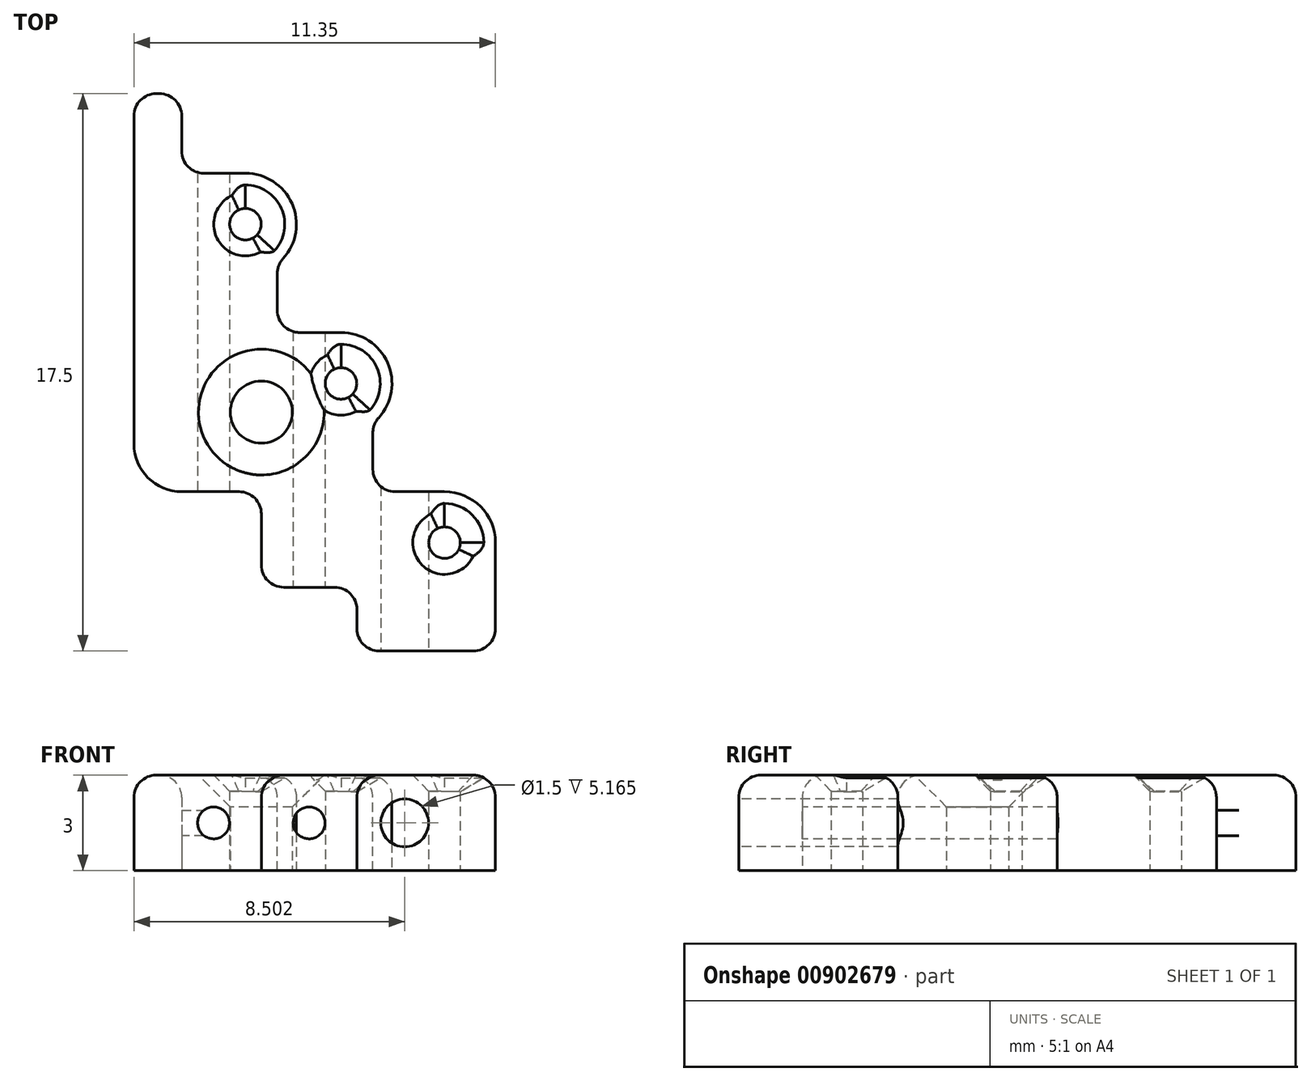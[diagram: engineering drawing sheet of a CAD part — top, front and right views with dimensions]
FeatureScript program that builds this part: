
annotation { "Feature Type Name" : "Feature", "Feature Type Description" : "" }
export const myFeature = defineFeature(function(context is Context, id is Id, definition is map)
    precondition{}
    {
        {
            var Q0;
            Q0=qCreatedBy(makeId("Top.planeOp"),FACE);
            var sketch = newSketch(context, id + "F0", { "sketchPlane" : qUnion([Q0])});
            skLineSegment(sketch, "E0.bottom", {"start": v(-17.84, 17.5) * mm, "end": v(-16.34, 17.5) * mm});
            skLineSegment(sketch, "E0.top", {"start": v(-10.84, 0) * mm, "end": v(-6.34, 0) * mm});
            skLineSegment(sketch, "E0.left", {"start": v(-17.84, 17.5) * mm, "end": v(-17.84, 6.5) * mm});
            skLineSegment(sketch, "E1", {"start": v(-14.34, 15) * mm, "end": v(-16.34, 15) * mm});
            skLineSegment(sketch, "E2", {"start": v(-13.34, 10) * mm, "end": v(-11.34, 10) * mm});
            skLineSegment(sketch, "E3", {"start": v(-10.34, 5) * mm, "end": v(-8.09, 5) * mm});
            skLineSegment(sketch, "E4", {"start": v(-9.34, 0) * mm, "end": v(-9.34, 5) * mm, "construction": true});
            skLineSegment(sketch, "E5", {"start": v(-12.34, 10) * mm, "end": v(-12.34, -0.79) * mm, "construction": true});
            skPoint(sketch, "E6.visualSharp", {"position": v(-6.34, 0) * mm});
            skLineSegment(sketch, "E7", {"start": v(-15.34, 0) * mm, "end": v(-15.34, 15) * mm, "construction": true});
            skLineSegment(sketch, "E8", {"start": v(-13.84, 2) * mm, "end": v(-10.84, 2) * mm});
            skLineSegment(sketch, "E9", {"start": v(-16.34, 5) * mm, "end": v(-13.84, 5) * mm});
            skLineSegment(sketch, "E10", {"start": v(-10.84, 2) * mm, "end": v(-10.84, 0) * mm});
            skLineSegment(sketch, "E11", {"start": v(-13.84, 5) * mm, "end": v(-13.84, 2) * mm});
            skCircle(sketch, "E12", {"center": v(-14.34, 13.4) * mm, "radius": 0.5 * mm});
            skPoint(sketch, "E13.visualSharp", {"position": v(-17.84, 17.5) * mm});
            skArc(sketch, "E14.filletArc", {"start": v(-17.84, 6.5) * mm, "mid": v(-17.4, 5.44) * mm, "end": v(-16.34, 5) * mm});
            skPoint(sketch, "E15.visualSharp", {"position": v(-10.84, 0) * mm});
            skCircle(sketch, "E16", {"center": v(-13.84, 7.5) * mm, "radius": 0.97 * mm});
            skCircle(sketch, "E17", {"center": v(-13.84, 7.5) * mm, "radius": 1.8 * mm, "construction": true});
            skLineSegment(sketch, "E18", {"start": v(-16.34, 15) * mm, "end": v(-16.34, 17.5) * mm});
            skLineSegment(sketch, "E19", {"start": v(-13.34, 10) * mm, "end": v(-13.34, 12.15) * mm});
            skLineSegment(sketch, "E20", {"start": v(-10.34, 5) * mm, "end": v(-10.34, 7.15) * mm});
            skCircle(sketch, "E21", {"center": v(-8.09, 3.4) * mm, "radius": 0.5 * mm});
            skLineSegment(sketch, "E22.trimOffspring", {"start": v(-6.49, 3.4) * mm, "end": v(-6.49, 0) * mm});
            skArc(sketch, "E23", {"start": v(-6.49, 3.4) * mm, "mid": v(-6.96, 4.53) * mm, "end": v(-8.09, 5) * mm});
            skCircle(sketch, "E24", {"center": v(-11.34, 8.4) * mm, "radius": 0.5 * mm});
            skArc(sketch, "E25", {"start": v(-10.34, 7.15) * mm, "mid": v(-9.83, 8.93) * mm, "end": v(-11.34, 10) * mm});
            skArc(sketch, "E26", {"start": v(-13.34, 12.15) * mm, "mid": v(-12.83, 13.93) * mm, "end": v(-14.34, 15) * mm});
            skSolve(sketch);
        }
        {
            var Q0;
            Q0=makeQuery(id+"F0.imprint","IMPRINT",FACE,{"disambiguationData":[TD([[makeQuery(id+"F0.imprint","IMPRINT",EDGE,{"derivedFrom":sQuery(id+"F0.wireOp",EDGE,"E0.bottom")}),-1.0]])]});
            extrude(context, id + "F1", {"entities" : qUnion([Q0]), "depth" : 3 * mm, "offsetDistance" : 25 * mm});
        }
        {
            var Q0;
            Q0=qCreatedBy(makeId("Front.planeOp"),FACE);
            var sketch = newSketch(context, id + "F2", { "sketchPlane" : qUnion([Q0])});
            skLineSegment(sketch, "E27.direction1", {"start": v(-9.34, 1.5) * mm, "end": v(-12.34, 1.5) * mm, "construction": true});
            skCircle(sketch, "E28", {"center": v(-9.34, 1.5) * mm, "radius": 0.75 * mm});
            skCircle(sketch, "E29", {"center": v(-12.34, 1.5) * mm, "radius": 0.5 * mm});
            skCircle(sketch, "E30.1.0.0", {"center": v(-15.34, 1.5) * mm, "radius": 0.5 * mm});
            skLineSegment(sketch, "E30.direction1", {"start": v(-12.34, 1.5) * mm, "end": v(-15.34, 1.5) * mm, "construction": true});
            skSolve(sketch);
        }
        {
            var Q0;
            Q0=makeQuery(id+"F2.imprint","IMPRINT",FACE,{"disambiguationData":[TD([[makeQuery(id+"F2.imprint","IMPRINT",EDGE,{"derivedFrom":sQuery(id+"F2.wireOp",EDGE,"E30.1.0.0")}),1.0]])]});
            extrude(context, id + "F3", {"entities" : qUnion([Q0]), "operationType" : NewBodyOperationType.REMOVE, "oppositeDirection" : true, "depth" : 25 * mm, "offsetDistance" : 25 * mm});
        }
        {
            var Q0;
            Q0=makeQuery(id+"F1.opExtrude","SWEPT_EDGE",EDGE,{"disambiguationData":[OSD([sQuery(id+"F0.wireOp",EDGE,"E0.bottom"),sQuery(id+"F0.wireOp",EDGE,"E18")])]});
            var Q1;
            Q1=makeQuery(id+"F1.opExtrude","SWEPT_EDGE",EDGE,{"disambiguationData":[OSD([sQuery(id+"F0.wireOp",EDGE,"E1"),sQuery(id+"F0.wireOp",EDGE,"E18")])]});
            var Q2;
            Q2=makeQuery(id+"F1.opExtrude","SWEPT_EDGE",EDGE,{"disambiguationData":[OSD([sQuery(id+"F0.wireOp",EDGE,"E19"),sQuery(id+"F0.wireOp",EDGE,"94513b36-e973-4ffa-a5f9-f9be3b932b12.trimOffspring")])]});
            var Q3;
            Q3=makeQuery(id+"F1.opExtrude","SWEPT_EDGE",EDGE,{"disambiguationData":[OSD([sQuery(id+"F0.wireOp",EDGE,"E1"),sQuery(id+"F0.wireOp",EDGE,"94513b36-e973-4ffa-a5f9-f9be3b932b12.trimOffspring")])]});
            var Q4;
            Q4=makeQuery(id+"F1.opExtrude","SWEPT_EDGE",EDGE,{"disambiguationData":[OSD([sQuery(id+"F0.wireOp",EDGE,"E2"),sQuery(id+"F0.wireOp",EDGE,"E25")])]});
            var Q5;
            Q5=makeQuery(id+"F1.opExtrude","SWEPT_EDGE",EDGE,{"disambiguationData":[OSD([sQuery(id+"F0.wireOp",EDGE,"E2"),sQuery(id+"F0.wireOp",EDGE,"E19")])]});
            var Q6;
            Q6=makeQuery(id+"F1.opExtrude","SWEPT_EDGE",EDGE,{"disambiguationData":[OSD([sQuery(id+"F0.wireOp",EDGE,"E20"),sQuery(id+"F0.wireOp",EDGE,"E25")])]});
            var Q7;
            Q7=makeQuery(id+"F1.opExtrude","SWEPT_EDGE",EDGE,{"disambiguationData":[OSD([sQuery(id+"F0.wireOp",EDGE,"E3"),sQuery(id+"F0.wireOp",EDGE,"E20")])]});
            var Q8;
            Q8=makeQuery(id+"F1.opExtrude","SWEPT_EDGE",EDGE,{"disambiguationData":[OSD([sQuery(id+"F0.wireOp",EDGE,"E22.trimOffspring"),sQuery(id+"F0.wireOp",EDGE,"E23")])]});
            var Q9;
            Q9=makeQuery(id+"F1.opExtrude","SWEPT_EDGE",EDGE,{"disambiguationData":[OSD([sQuery(id+"F0.wireOp",EDGE,"E0.top"),sQuery(id+"F0.wireOp",EDGE,"E22.trimOffspring")])]});
            var Q10;
            Q10=makeQuery(id+"F1.opExtrude","SWEPT_EDGE",EDGE,{"disambiguationData":[OSD([sQuery(id+"F0.wireOp",EDGE,"E0.top"),sQuery(id+"F0.wireOp",EDGE,"E10")])]});
            var Q11;
            Q11=makeQuery(id+"F1.opExtrude","SWEPT_EDGE",EDGE,{"disambiguationData":[OSD([sQuery(id+"F0.wireOp",EDGE,"E8"),sQuery(id+"F0.wireOp",EDGE,"E10")])]});
            var Q12;
            Q12=makeQuery(id+"F1.opExtrude","SWEPT_EDGE",EDGE,{"disambiguationData":[OSD([sQuery(id+"F0.wireOp",EDGE,"E8"),sQuery(id+"F0.wireOp",EDGE,"E11")])]});
            var Q13;
            Q13=makeQuery(id+"F1.opExtrude","SWEPT_EDGE",EDGE,{"disambiguationData":[OSD([sQuery(id+"F0.wireOp",EDGE,"E9"),sQuery(id+"F0.wireOp",EDGE,"E11")])]});
            var Q14;
            Q14=makeQuery(id+"F1.opExtrude","SWEPT_EDGE",EDGE,{"disambiguationData":[OSD([sQuery(id+"F0.wireOp",EDGE,"E0.bottom"),sQuery(id+"F0.wireOp",EDGE,"E0.left")])]});
            fillet(context, id + "F4", {"entities" : qUnion([Q0, Q1, Q2, Q3, Q4, Q5, Q6, Q7, Q8, Q9, Q10, Q11, Q12, Q13, Q14]), "radius" : 0.7 * mm, "tangentPropagation" : true, "allowEdgeOverflow" : false});
        }
        {
            var Q0;
            Q0=makeQuery(id+"F1.opExtrude","CAP_EDGE",EDGE,{"disambiguationData":[OSD([sQuery(id+"F0.wireOp",EDGE,"E0.left")])],"isStart":false});
            fillet(context, id + "F5", {"entities" : qUnion([Q0]), "radius" : 0.7 * mm, "tangentPropagation" : true, "allowEdgeOverflow" : false});
        }
        {
            var Q0;
            Q0=makeQuery(id+"F1.opExtrude","CAP_EDGE",EDGE,{"disambiguationData":[OSD([sQuery(id+"F0.wireOp",EDGE,"E16")])],"isStart":false});
            chamfer(context, id + "F6", {"entities" : qUnion([Q0]), "width" : 1 * mm, "tangentPropagation" : true});
        }
        {
            var Q0;
            Q0=makeQuery(id+"F1.opExtrude","CAP_EDGE",EDGE,{"disambiguationData":[OSD([sQuery(id+"F0.wireOp",EDGE,"E24")])],"isStart":false});
            var Q1;
            Q1=makeQuery(id+"F1.opExtrude","CAP_EDGE",EDGE,{"disambiguationData":[OSD([sQuery(id+"F0.wireOp",EDGE,"E12")])],"isStart":false});
            var Q2;
            Q2=makeQuery(id+"F1.opExtrude","CAP_EDGE",EDGE,{"disambiguationData":[OSD([sQuery(id+"F0.wireOp",EDGE,"E21")])],"isStart":false});
            chamfer(context, id + "F7", {"entities" : qUnion([Q0, Q1, Q2]), "width" : 0.5 * mm, "tangentPropagation" : true});
        }
        {
            var Q0;
            Q0=makeQuery(id+"F2.imprint","IMPRINT",FACE,{"disambiguationData":[TD([[makeQuery(id+"F2.imprint","IMPRINT",EDGE,{"derivedFrom":sQuery(id+"F2.wireOp",EDGE,"E28")}),1.0]])]});
            extrude(context, id + "F8", {"entities" : qUnion([Q0]), "operationType" : NewBodyOperationType.REMOVE, "oppositeDirection" : true, "depth" : 6 * mm, "offsetDistance" : 25 * mm});
        }
        {
            var Q0;
            Q0=makeQuery(id+"F2.imprint","IMPRINT",FACE,{"disambiguationData":[TD([[makeQuery(id+"F2.imprint","IMPRINT",EDGE,{"derivedFrom":sQuery(id+"F2.wireOp",EDGE,"E29")}),1.0]])]});
            extrude(context, id + "F9", {"entities" : qUnion([Q0]), "operationType" : NewBodyOperationType.REMOVE, "oppositeDirection" : true, "depth" : 11 * mm, "offsetDistance" : 25 * mm});
        }
    });
